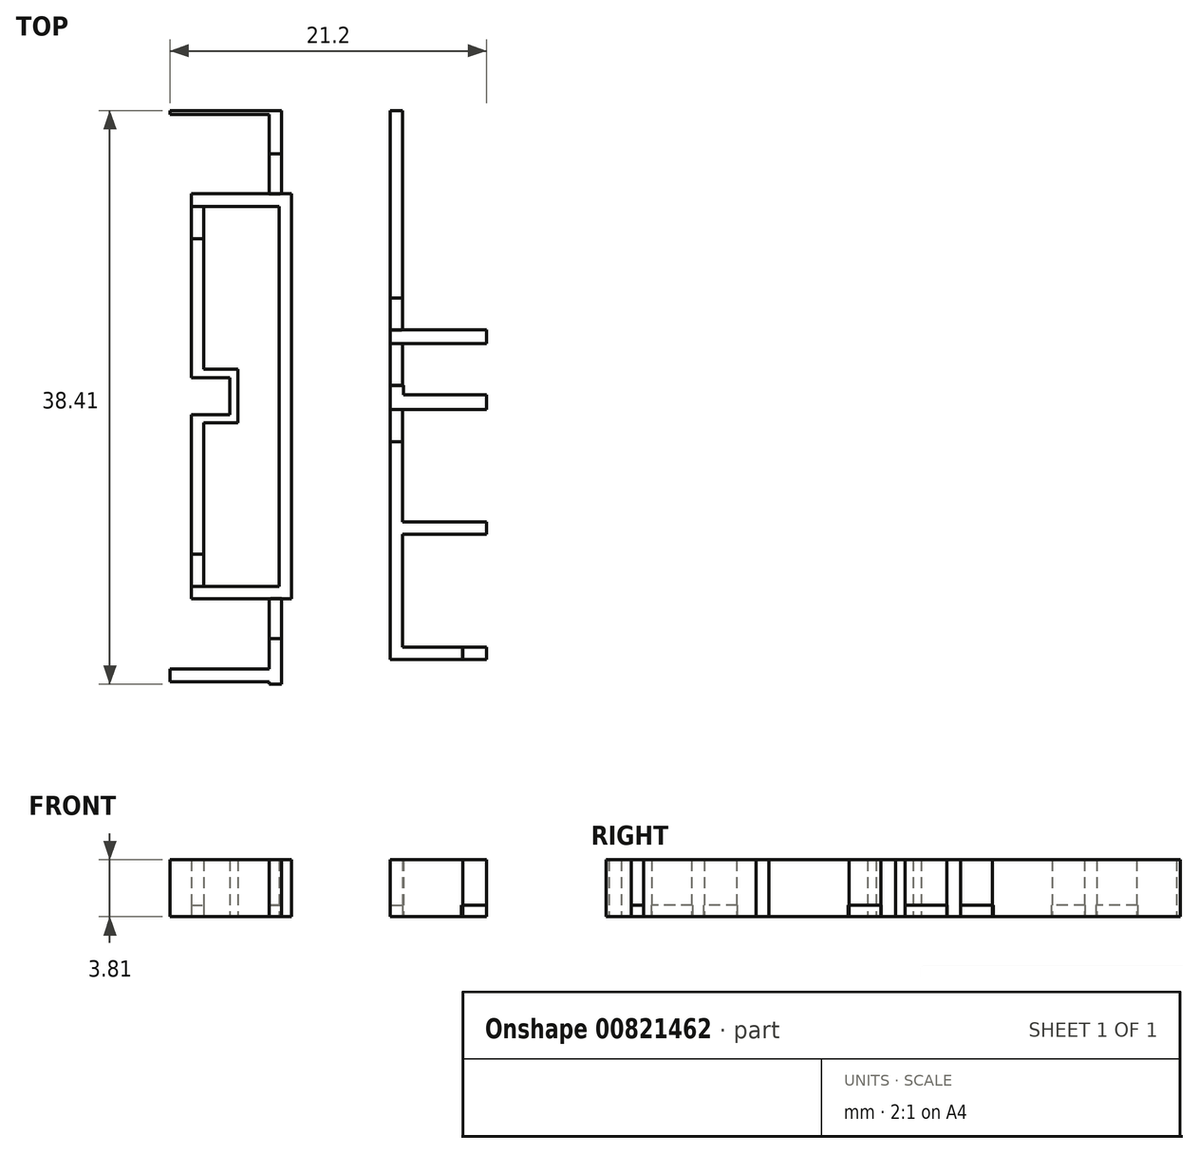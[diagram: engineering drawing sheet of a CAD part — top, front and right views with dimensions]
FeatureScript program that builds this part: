
annotation { "Feature Type Name" : "Feature", "Feature Type Description" : "" }
export const myFeature = defineFeature(function(context is Context, id is Id, definition is map)
    precondition{}
    {
        {
            var Q0;
            Q0=qCreatedBy(makeId("Top.planeOp"),FACE);
            var sketch = newSketch(context, id + "F0", { "sketchPlane" : qUnion([Q0])});
            skLineSegment(sketch, "E0.bottom", {"start": v(-47.5, 0.72) * mm, "end": v(-48.34, 0.72) * mm});
            skLineSegment(sketch, "E0.top", {"start": v(-47.5, -2.2) * mm, "end": v(-48.34, -2.2) * mm});
            skLineSegment(sketch, "E0.left", {"start": v(-47.5, 0.72) * mm, "end": v(-47.5, -2.2) * mm});
            skLineSegment(sketch, "E0.right", {"start": v(-48.34, 0.72) * mm, "end": v(-48.34, -2.2) * mm});
            skLineSegment(sketch, "E1.bottom", {"start": v(-48.34, 0.72) * mm, "end": v(-54.97, 0.72) * mm});
            skLineSegment(sketch, "E1.top", {"start": v(-48.34, 0.46) * mm, "end": v(-54.97, 0.46) * mm});
            skLineSegment(sketch, "E1.left", {"start": v(-48.34, 0.72) * mm, "end": v(-48.34, 0.46) * mm});
            skLineSegment(sketch, "E1.right", {"start": v(-54.97, 0.72) * mm, "end": v(-54.97, 0.46) * mm});
            skLineSegment(sketch, "E2.bottom", {"start": v(-40.23, 0.72) * mm, "end": v(-39.4, 0.72) * mm});
            skLineSegment(sketch, "E2.top", {"start": v(-40.23, -11.84) * mm, "end": v(-39.4, -11.84) * mm});
            skLineSegment(sketch, "E2.left", {"start": v(-40.23, 0.72) * mm, "end": v(-40.23, -11.84) * mm});
            skLineSegment(sketch, "E2.right", {"start": v(-39.4, 0.72) * mm, "end": v(-39.4, -11.84) * mm});
            skLineSegment(sketch, "E3.bottom", {"start": v(-33.79, -13.97) * mm, "end": v(-40.23, -13.97) * mm});
            skLineSegment(sketch, "E3.top", {"start": v(-33.79, -14.9) * mm, "end": v(-40.23, -14.9) * mm});
            skLineSegment(sketch, "E3.right", {"start": v(-40.23, -13.97) * mm, "end": v(-40.23, -14.9) * mm});
            skLineSegment(sketch, "E4.bottom", {"start": v(-35.38, -36.03) * mm, "end": v(-40.23, -36.03) * mm});
            skLineSegment(sketch, "E4.top", {"start": v(-35.38, -35.2) * mm, "end": v(-40.23, -35.2) * mm});
            skLineSegment(sketch, "E4.left", {"start": v(-35.38, -36.03) * mm, "end": v(-35.38, -35.2) * mm});
            skLineSegment(sketch, "E4.right", {"start": v(-40.23, -36.03) * mm, "end": v(-40.23, -35.2) * mm});
            skLineSegment(sketch, "E5.bottom", {"start": v(-40.23, -35.2) * mm, "end": v(-39.4, -35.2) * mm});
            skLineSegment(sketch, "E5.top", {"start": v(-40.23, -21.45) * mm, "end": v(-39.4, -21.45) * mm});
            skLineSegment(sketch, "E5.left", {"start": v(-40.23, -35.2) * mm, "end": v(-40.23, -21.45) * mm});
            skLineSegment(sketch, "E5.right", {"start": v(-39.4, -35.2) * mm, "end": v(-39.4, -21.45) * mm});
            skLineSegment(sketch, "E6.bottom", {"start": v(-39.4, -26.82) * mm, "end": v(-33.78, -26.82) * mm});
            skLineSegment(sketch, "E6.top", {"start": v(-39.4, -27.65) * mm, "end": v(-33.78, -27.65) * mm});
            skLineSegment(sketch, "E6.left", {"start": v(-39.4, -26.82) * mm, "end": v(-39.4, -27.65) * mm});
            skLineSegment(sketch, "E6.right", {"start": v(-33.78, -26.82) * mm, "end": v(-33.78, -27.65) * mm});
            skLineSegment(sketch, "E7.bottom", {"start": v(-39.35, -17.7) * mm, "end": v(-40.23, -17.7) * mm});
            skLineSegment(sketch, "E7.top", {"start": v(-39.35, -19.3) * mm, "end": v(-40.23, -19.3) * mm});
            skLineSegment(sketch, "E7.left", {"start": v(-39.35, -17.7) * mm, "end": v(-39.35, -19.3) * mm});
            skLineSegment(sketch, "E7.right", {"start": v(-40.23, -17.7) * mm, "end": v(-40.23, -19.3) * mm});
            skLineSegment(sketch, "E8.bottom", {"start": v(-39.35, -19.3) * mm, "end": v(-33.78, -19.3) * mm});
            skLineSegment(sketch, "E8.top", {"start": v(-39.35, -18.33) * mm, "end": v(-33.78, -18.33) * mm});
            skLineSegment(sketch, "E8.left", {"start": v(-39.35, -19.3) * mm, "end": v(-39.35, -18.33) * mm});
            skLineSegment(sketch, "E8.right", {"start": v(-33.78, -19.3) * mm, "end": v(-33.78, -18.33) * mm});
            skLineSegment(sketch, "E9.bottom", {"start": v(-53.54, -4.87) * mm, "end": v(-46.84, -4.87) * mm});
            skLineSegment(sketch, "E9.top", {"start": v(-53.54, -5.7) * mm, "end": v(-46.84, -5.7) * mm});
            skLineSegment(sketch, "E9.left", {"start": v(-53.54, -4.87) * mm, "end": v(-53.54, -5.7) * mm});
            skLineSegment(sketch, "E9.right", {"start": v(-46.84, -4.87) * mm, "end": v(-46.84, -5.7) * mm});
            skLineSegment(sketch, "E10.bottom", {"start": v(-53.54, -7.86) * mm, "end": v(-52.7, -7.86) * mm});
            skLineSegment(sketch, "E10.top", {"start": v(-53.54, -17.17) * mm, "end": v(-52.7, -17.17) * mm});
            skLineSegment(sketch, "E10.left", {"start": v(-53.54, -7.86) * mm, "end": v(-53.54, -17.17) * mm});
            skLineSegment(sketch, "E10.right", {"start": v(-52.7, -7.86) * mm, "end": v(-52.7, -17.17) * mm});
            skLineSegment(sketch, "E11.bottom", {"start": v(-52.7, -19.63) * mm, "end": v(-53.54, -19.63) * mm});
            skLineSegment(sketch, "E11.top", {"start": v(-52.7, -28.97) * mm, "end": v(-53.54, -28.97) * mm});
            skLineSegment(sketch, "E11.left", {"start": v(-52.7, -19.63) * mm, "end": v(-52.7, -28.97) * mm});
            skLineSegment(sketch, "E11.right", {"start": v(-53.54, -19.63) * mm, "end": v(-53.54, -28.97) * mm});
            skLineSegment(sketch, "E12.bottom", {"start": v(-53.54, -31.13) * mm, "end": v(-47.67, -31.13) * mm});
            skLineSegment(sketch, "E12.top", {"start": v(-53.54, -31.97) * mm, "end": v(-47.67, -31.97) * mm});
            skLineSegment(sketch, "E12.left", {"start": v(-53.54, -31.13) * mm, "end": v(-53.54, -31.97) * mm});
            skLineSegment(sketch, "E12.right", {"start": v(-47.67, -31.13) * mm, "end": v(-47.67, -31.97) * mm});
            skLineSegment(sketch, "E13.bottom", {"start": v(-47.67, -31.97) * mm, "end": v(-46.84, -31.97) * mm});
            skLineSegment(sketch, "E13.top", {"start": v(-47.67, -5.7) * mm, "end": v(-46.84, -5.7) * mm});
            skLineSegment(sketch, "E13.left", {"start": v(-47.67, -31.97) * mm, "end": v(-47.67, -5.7) * mm});
            skLineSegment(sketch, "E13.right", {"start": v(-46.84, -31.97) * mm, "end": v(-46.84, -5.7) * mm});
            skLineSegment(sketch, "E14.bottom", {"start": v(-48.34, -34.64) * mm, "end": v(-47.5, -34.64) * mm});
            skLineSegment(sketch, "E14.top", {"start": v(-48.34, -37.7) * mm, "end": v(-47.5, -37.7) * mm});
            skLineSegment(sketch, "E14.left", {"start": v(-48.34, -34.64) * mm, "end": v(-48.34, -37.7) * mm});
            skLineSegment(sketch, "E14.right", {"start": v(-47.5, -34.64) * mm, "end": v(-47.5, -37.7) * mm});
            skLineSegment(sketch, "E15.bottom", {"start": v(-54.98, -36.68) * mm, "end": v(-48.34, -36.68) * mm});
            skLineSegment(sketch, "E15.top", {"start": v(-54.98, -37.52) * mm, "end": v(-48.34, -37.52) * mm});
            skLineSegment(sketch, "E15.right", {"start": v(-48.34, -36.68) * mm, "end": v(-48.34, -37.52) * mm});
            skLineSegment(sketch, "E16", {"start": v(-54.97, 0.72) * mm, "end": v(-33.79, 0.72) * mm});
            skLineSegment(sketch, "E17", {"start": v(-33.79, 0.72) * mm, "end": v(-33.79, -37.7) * mm});
            skLineSegment(sketch, "E18", {"start": v(-54.98, -36.68) * mm, "end": v(-54.98, -37.52) * mm});
            skLineSegment(sketch, "E19", {"start": v(-33.79, -13.97) * mm, "end": v(-33.79, -14.9) * mm});
            skLineSegment(sketch, "E20.bottom", {"start": v(-52.7, -17.17) * mm, "end": v(-50.42, -17.17) * mm});
            skLineSegment(sketch, "E20.top", {"start": v(-52.7, -16.61) * mm, "end": v(-50.42, -16.61) * mm});
            skLineSegment(sketch, "E20.left", {"start": v(-52.7, -17.17) * mm, "end": v(-52.7, -16.61) * mm});
            skLineSegment(sketch, "E20.right", {"start": v(-50.42, -17.17) * mm, "end": v(-50.42, -16.61) * mm});
            skLineSegment(sketch, "E21.bottom", {"start": v(-52.7, -19.63) * mm, "end": v(-50.42, -19.63) * mm});
            skLineSegment(sketch, "E21.top", {"start": v(-52.7, -20.2) * mm, "end": v(-50.42, -20.2) * mm});
            skLineSegment(sketch, "E21.left", {"start": v(-52.7, -19.63) * mm, "end": v(-52.7, -20.2) * mm});
            skLineSegment(sketch, "E21.right", {"start": v(-50.42, -19.63) * mm, "end": v(-50.42, -20.2) * mm});
            skLineSegment(sketch, "E22.bottom", {"start": v(-50.42, -17.17) * mm, "end": v(-50.98, -17.17) * mm});
            skLineSegment(sketch, "E22.top", {"start": v(-50.42, -19.63) * mm, "end": v(-50.98, -19.63) * mm});
            skLineSegment(sketch, "E22.left", {"start": v(-50.42, -17.17) * mm, "end": v(-50.42, -19.63) * mm});
            skLineSegment(sketch, "E22.right", {"start": v(-50.98, -17.17) * mm, "end": v(-50.98, -19.63) * mm});
            skSolve(sketch);
        }
        {
            var Q0;
            Q0 = qSketchRegion(id + "F0", true);
            extrude(context, id + "F1", {"entities" : qUnion([Q0]), "depth" : 3.8 * mm, "offsetDistance" : 25.4 * mm});
        }
        {
            var Q0;
            Q0=qCreatedBy(makeId("Top.planeOp"),FACE);
            var sketch = newSketch(context, id + "F2", { "sketchPlane" : qUnion([Q0])});
            skLineSegment(sketch, "E23.bottom", {"start": v(-40.23, -11.79) * mm, "end": v(-39.4, -11.79) * mm});
            skLineSegment(sketch, "E23.top", {"start": v(-40.23, -14.03) * mm, "end": v(-39.4, -14.03) * mm});
            skLineSegment(sketch, "E23.left", {"start": v(-40.23, -11.79) * mm, "end": v(-40.23, -14.03) * mm});
            skLineSegment(sketch, "E23.right", {"start": v(-39.4, -11.79) * mm, "end": v(-39.4, -14.03) * mm});
            skLineSegment(sketch, "E24.bottom", {"start": v(-40.23, -14.85) * mm, "end": v(-39.4, -14.85) * mm});
            skLineSegment(sketch, "E24.top", {"start": v(-40.23, -17.74) * mm, "end": v(-39.4, -17.74) * mm});
            skLineSegment(sketch, "E24.left", {"start": v(-40.23, -14.85) * mm, "end": v(-40.23, -17.74) * mm});
            skLineSegment(sketch, "E24.right", {"start": v(-39.4, -14.85) * mm, "end": v(-39.4, -17.74) * mm});
            skLineSegment(sketch, "E25.bottom", {"start": v(-53.54, -5.65) * mm, "end": v(-52.7, -5.65) * mm});
            skLineSegment(sketch, "E25.top", {"start": v(-53.54, -7.91) * mm, "end": v(-52.7, -7.91) * mm});
            skLineSegment(sketch, "E25.left", {"start": v(-53.54, -5.65) * mm, "end": v(-53.54, -7.91) * mm});
            skLineSegment(sketch, "E25.right", {"start": v(-52.7, -5.65) * mm, "end": v(-52.7, -7.91) * mm});
            skLineSegment(sketch, "E26.bottom", {"start": v(-53.54, -28.92) * mm, "end": v(-52.7, -28.92) * mm});
            skLineSegment(sketch, "E26.top", {"start": v(-53.54, -31.18) * mm, "end": v(-52.7, -31.18) * mm});
            skLineSegment(sketch, "E26.left", {"start": v(-53.54, -28.92) * mm, "end": v(-53.54, -31.18) * mm});
            skLineSegment(sketch, "E26.right", {"start": v(-52.7, -28.92) * mm, "end": v(-52.7, -31.18) * mm});
            skLineSegment(sketch, "E27.bottom", {"start": v(-35.48, -35.2) * mm, "end": v(-33.79, -35.2) * mm});
            skLineSegment(sketch, "E27.top", {"start": v(-35.48, -36.03) * mm, "end": v(-33.79, -36.03) * mm});
            skLineSegment(sketch, "E27.left", {"start": v(-35.48, -35.2) * mm, "end": v(-35.48, -36.03) * mm});
            skLineSegment(sketch, "E27.right", {"start": v(-33.79, -35.2) * mm, "end": v(-33.79, -36.03) * mm});
            skLineSegment(sketch, "E28.bottom", {"start": v(-40.23, -19.26) * mm, "end": v(-39.4, -19.26) * mm});
            skLineSegment(sketch, "E28.top", {"start": v(-40.23, -21.5) * mm, "end": v(-39.4, -21.5) * mm});
            skLineSegment(sketch, "E28.left", {"start": v(-40.23, -19.26) * mm, "end": v(-40.23, -21.5) * mm});
            skLineSegment(sketch, "E28.right", {"start": v(-39.4, -19.26) * mm, "end": v(-39.4, -21.5) * mm});
            skLineSegment(sketch, "E29.bottom", {"start": v(-48.33, -2.15) * mm, "end": v(-47.5, -2.15) * mm});
            skLineSegment(sketch, "E29.top", {"start": v(-48.33, -4.92) * mm, "end": v(-47.5, -4.92) * mm});
            skLineSegment(sketch, "E29.left", {"start": v(-48.33, -2.15) * mm, "end": v(-48.33, -4.92) * mm});
            skLineSegment(sketch, "E29.right", {"start": v(-47.5, -2.15) * mm, "end": v(-47.5, -4.92) * mm});
            skLineSegment(sketch, "E30.bottom", {"start": v(-47.5, -31.92) * mm, "end": v(-48.34, -31.92) * mm});
            skLineSegment(sketch, "E30.top", {"start": v(-47.5, -34.69) * mm, "end": v(-48.34, -34.69) * mm});
            skLineSegment(sketch, "E30.left", {"start": v(-47.5, -31.92) * mm, "end": v(-47.5, -34.69) * mm});
            skLineSegment(sketch, "E30.right", {"start": v(-48.34, -31.92) * mm, "end": v(-48.34, -34.69) * mm});
            skSolve(sketch);
        }
        {
            var Q0;
            Q0 = qSketchRegion(id + "F2", true);
            extrude(context, id + "F3", {"entities" : qUnion([Q0]), "depth" : 0.76 * mm, "offsetDistance" : 25.4 * mm});
        }
    });
